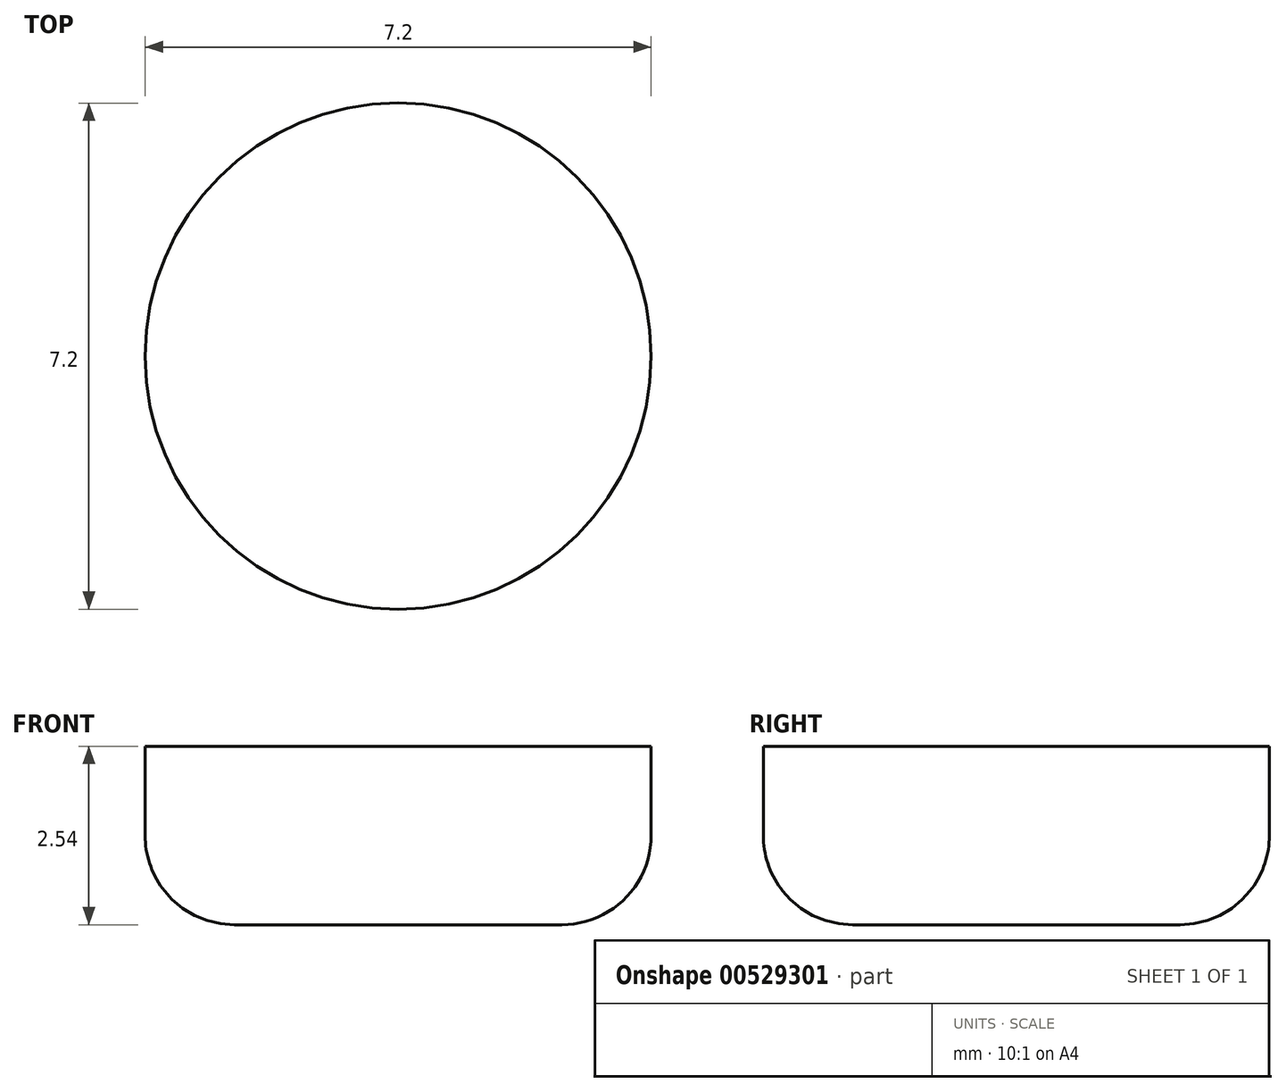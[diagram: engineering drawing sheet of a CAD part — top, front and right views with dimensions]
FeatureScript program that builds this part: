
annotation { "Feature Type Name" : "Feature", "Feature Type Description" : "" }
export const myFeature = defineFeature(function(context is Context, id is Id, definition is map)
    precondition{}
    {
        {
            var Q0;
            Q0=qCreatedBy(makeId("Top.planeOp"),FACE);
            var sketch = newSketch(context, id + "F0", { "sketchPlane" : qUnion([Q0])});
            skCircle(sketch, "E0", {"center": v(0, 0) * mm, "radius": 3.6 * mm});
            skSolve(sketch);
        }
        {
            var Q0;
            Q0 = qSketchRegion(id + "F0", true);
            extrude(context, id + "F1", {"entities" : qUnion([Q0]), "oppositeDirection" : true, "depth" : 2.54 * mm, "offsetDistance" : 25.4 * mm});
        }
        {
            var Q0;
            Q0=makeQuery(id+"F1.opExtrude","CAP_EDGE",EDGE,{"disambiguationData":[OSD([sQuery(id+"F0.wireOp",EDGE,"E0")])],"isStart":false});
            fillet(context, id + "F2", {"entities" : qUnion([Q0]), "radius" : 1.27 * mm, "tangentPropagation" : true, "allowEdgeOverflow" : false});
        }
    });
